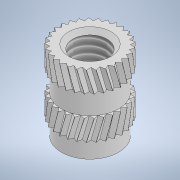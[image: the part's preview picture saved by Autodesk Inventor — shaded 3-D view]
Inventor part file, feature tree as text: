
AUTODESK INVENTOR PART (.ipt)
format: ipt  version: 2022 (Build 260153000, 153)  size: 741,376 bytes
history: native  units: mm
features: sketch x4, revolve x1, loft x1, pattern_circular x1, plane x1, mirror x1, hole x1, chamfer x1, projected_geometry x1
ambient origin geometry x8: Origin, YZ Plane, XZ Plane, XY Plane, X Axis, Y Axis, Z Axis, Center Point
bodies: Solid1 (feature_tree)
feature tree (12):
  revolve  "Revolution1"  [1 undecoded]
  loft  "Loft2"
  pattern_circular  "Circular Pattern2"  Angle=90.0deg  [1 undecoded]
  plane  "Work Plane1"
  mirror  "Mirror1"
  hole  "Hole1"  [1 undecoded]
  chamfer  "Chamfer1"  Distance=0.25mm
  sketch  "Sketch1"  dims[d0=2.3mm d1=5.7mm]
  sketch  "Sketch2"  dims[d2=0.25mm d3=1.5mm]
  projected_geometry  "Projected Loop1"
  sketch  "Sketch3"  dims[d4=1.5mm]
  sketch  "Sketch4"  dims[d5=1.5mm d6=90.0deg d16=0.5mm d17=0.25mm d18=0.5mm d19=0.25mm d20=0.0mm d21=90.0deg d22=0.0mm d23=90.0deg d24=0.1mm d25=0.1mm d26=1.745329mm d30=290.0mm d31=360.0deg d33=2.459mm d34=6.0mm d35=6.3mm d36=2.0mm d37=90.0deg d38=8.0mm d39=20.594885mm d40=0.3mm d41=2.0mm d42=45.0deg]
note: 3 required parameter values undecoded (feature->parameter linkage not recoverable at this tier; creation-order binding heuristic only, values carry confidence <= 0.55)